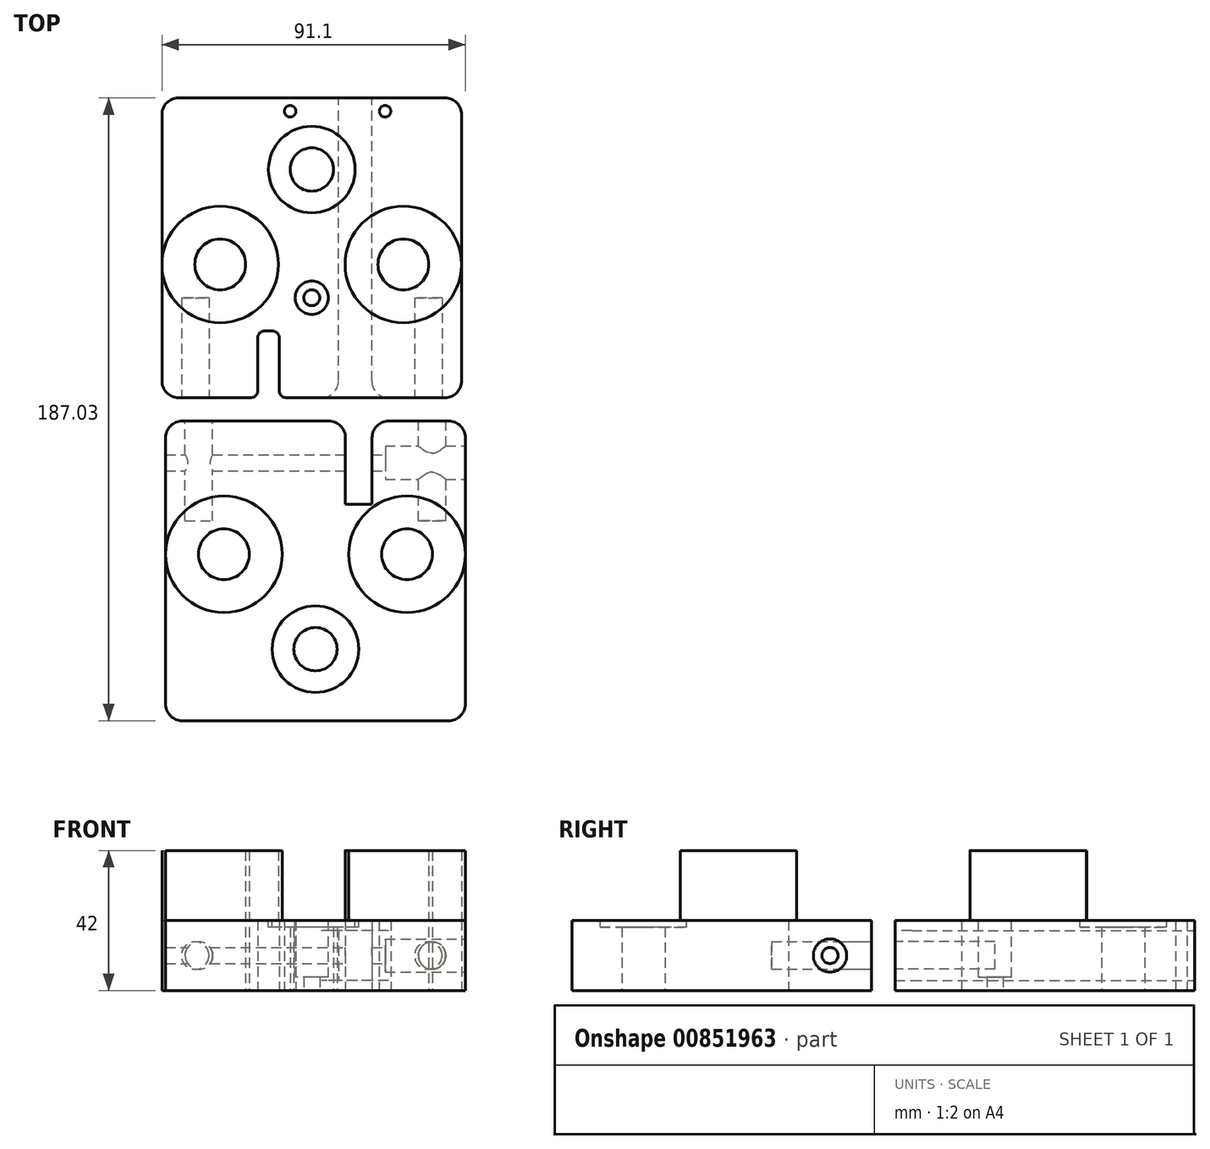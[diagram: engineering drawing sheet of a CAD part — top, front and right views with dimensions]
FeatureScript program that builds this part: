
annotation { "Feature Type Name" : "Feature", "Feature Type Description" : "" }
export const myFeature = defineFeature(function(context is Context, id is Id, definition is map)
    precondition{}
    {
        {
            var Q0;
            Q0=qCreatedBy(makeId("Top.planeOp"),FACE);
            var sketch = newSketch(context, id + "F0", { "sketchPlane" : qUnion([Q0])});
            skLineSegment(sketch, "E0", {"start": v(27.5, 0) * mm, "end": v(-27.5, 0) * mm, "construction": true});
            skCircle(sketch, "E1", {"center": v(-27.5, 0) * mm, "radius": 7.62 * mm});
            skCircle(sketch, "E2", {"center": v(27.5, 0) * mm, "radius": 7.62 * mm});
            skLineSegment(sketch, "E3", {"start": v(0, 28.5) * mm, "end": v(0, -10) * mm, "construction": true});
            skCircle(sketch, "E4", {"center": v(0, 28.5) * mm, "radius": 6.5 * mm});
            skCircle(sketch, "E5", {"center": v(0, 28.5) * mm, "radius": 13 * mm, "construction": true});
            skCircle(sketch, "E6", {"center": v(0, -10) * mm, "radius": 2.4 * mm});
            skCircle(sketch, "E7", {"center": v(0, -10) * mm, "radius": 5 * mm, "construction": true});
            skLineSegment(sketch, "E8", {"start": v(-45, -40) * mm, "end": v(-16.25, -40) * mm});
            skLineSegment(sketch, "E9", {"start": v(0, -10) * mm, "end": v(0, -40) * mm, "construction": true});
            skLineSegment(sketch, "E10", {"start": v(35, -40) * mm, "end": v(35, -10) * mm, "construction": true});
            skLineSegment(sketch, "E11", {"start": v(-35, -40) * mm, "end": v(-35, -10) * mm, "construction": true});
            skLineSegment(sketch, "E12", {"start": v(-45, -40) * mm, "end": v(-45, 50) * mm});
            skLineSegment(sketch, "E13", {"start": v(45, -40) * mm, "end": v(45, 50) * mm});
            skLineSegment(sketch, "E14", {"start": v(13, -40) * mm, "end": v(13, 50) * mm, "construction": true});
            skLineSegment(sketch, "E15", {"start": v(-13, -40) * mm, "end": v(-13, 50) * mm, "construction": true});
            skLineSegment(sketch, "E16", {"start": v(-45, 50) * mm, "end": v(45, 50) * mm});
            skLineSegment(sketch, "E17", {"start": v(-6.5, 46) * mm, "end": v(22, 46) * mm, "construction": true});
            skCircle(sketch, "E18", {"center": v(22, 46) * mm, "radius": 1.72 * mm});
            skCircle(sketch, "E19", {"center": v(-6.5, 46) * mm, "radius": 1.72 * mm});
            skLineSegment(sketch, "E20", {"start": v(-9.75, -20) * mm, "end": v(-16.25, -20) * mm});
            skPoint(sketch, "E21", {"position": v(-13, -20) * mm});
            skLineSegment(sketch, "E22", {"start": v(-16.25, -20) * mm, "end": v(-16.25, -40) * mm});
            skLineSegment(sketch, "E23", {"start": v(-9.75, -20) * mm, "end": v(-9.75, -40) * mm});
            skLineSegment(sketch, "E24.trimOffspring", {"start": v(-9.75, -40) * mm, "end": v(45, -40) * mm});
            skSolve(sketch);
        }
        {
            var Q0;
            Q0 = qSketchRegion(id + "F0", true);
            extrude(context, id + "F1", {"entities" : qUnion([Q0]), "depth" : 21 * mm, "offsetDistance" : 25 * mm});
        }
        {
            var Q0;
            Q0=makeQuery(id+"F1.opExtrude","CAP_FACE",FACE,{"disambiguationData":[OSD([sQuery(id+"F0.wireOp",EDGE,"E1"),sQuery(id+"F0.wireOp",EDGE,"E2"),sQuery(id+"F0.wireOp",EDGE,"E5"),sQuery(id+"F0.wireOp",EDGE,"E6"),sQuery(id+"F0.wireOp",EDGE,"E8"),sQuery(id+"F0.wireOp",EDGE,"E12"),sQuery(id+"F0.wireOp",EDGE,"E13"),sQuery(id+"F0.wireOp",EDGE,"E16"),sQuery(id+"F0.wireOp",EDGE,"E18"),sQuery(id+"F0.wireOp",EDGE,"E19")])],"isStart":false});
            var sketch = newSketch(context, id + "F2", { "sketchPlane" : qUnion([Q0])});
            skCircle(sketch, "E25.0", {"center": v(0, -10) * mm, "radius": 5 * mm});
            skSolve(sketch);
        }
        {
            var Q0;
            Q0=makeQuery(id+"F2.imprint","IMPRINT",FACE,{"disambiguationData":[TD([[makeQuery(id+"F2.imprint","IMPRINT",EDGE,{"derivedFrom":sQuery(id+"F2.wireOp",EDGE,"E25.0")}),1.0]])]});
            extrude(context, id + "F3", {"entities" : qUnion([Q0]), "operationType" : NewBodyOperationType.REMOVE, "oppositeDirection" : true, "depth" : 17 * mm, "offsetDistance" : 25 * mm});
        }
        {
            var Q0;
            Q0=makeQuery(id+"F1.opExtrude","CAP_FACE",FACE,{"disambiguationData":[OSD([sQuery(id+"F0.wireOp",EDGE,"E1"),sQuery(id+"F0.wireOp",EDGE,"E2"),sQuery(id+"F0.wireOp",EDGE,"E4"),sQuery(id+"F0.wireOp",EDGE,"E6"),sQuery(id+"F0.wireOp",EDGE,"E8"),sQuery(id+"F0.wireOp",EDGE,"E12"),sQuery(id+"F0.wireOp",EDGE,"E13"),sQuery(id+"F0.wireOp",EDGE,"E16"),sQuery(id+"F0.wireOp",EDGE,"E18"),sQuery(id+"F0.wireOp",EDGE,"E19")])],"isStart":false});
            var sketch = newSketch(context, id + "F4", { "sketchPlane" : qUnion([Q0])});
            skCircle(sketch, "E26.0", {"center": v(0, 28.5) * mm, "radius": 13 * mm});
            skPoint(sketch, "E27.0", {"position": v(-27.5, 0) * mm});
            skPoint(sketch, "E27.1", {"position": v(27.5, 0) * mm});
            skCircle(sketch, "E28", {"center": v(-27.5, 0) * mm, "radius": 17.5 * mm});
            skCircle(sketch, "E29", {"center": v(27.5, 0) * mm, "radius": 17.49 * mm});
            skLineSegment(sketch, "E30.0", {"start": v(45, -40) * mm, "end": v(45, 50) * mm});
            skSolve(sketch);
        }
        {
            var Q0;
            Q0=makeQuery(id+"F4.imprint","IMPRINT",FACE,{"disambiguationData":[TD([[makeQuery(id+"F4.imprint","IMPRINT",EDGE,{"derivedFrom":sQuery(id+"F4.wireOp",EDGE,"E28")}),1.0]])]});
            var Q1;
            Q1=makeQuery(id+"F4.imprint","IMPRINT",FACE,{"disambiguationData":[TD([[makeQuery(id+"F4.imprint","IMPRINT",EDGE,{"derivedFrom":makeQuery(id+"F1.opExtrude","CAP_EDGE",EDGE,{"disambiguationData":[OSD([sQuery(id+"F0.wireOp",EDGE,"E2")])],"isStart":false})}),-1.0]])]});
            extrude(context, id + "F5", {"entities" : qUnion([Q0, Q1]), "operationType" : NewBodyOperationType.ADD, "depth" : 21 * mm, "offsetDistance" : 25 * mm});
        }
        {
            var Q0;
            Q0=makeQuery(id+"F1.opExtrude","SWEPT_FACE",FACE,{"disambiguationData":[OSD([sQuery(id+"F0.wireOp",EDGE,"E16")])]});
            var sketch = newSketch(context, id + "F6", { "sketchPlane" : qUnion([Q0])});
            skPoint(sketch, "E31.0", {"position": v(-13, 0) * mm});
            skLineSegment(sketch, "E32.bottom", {"start": v(-18, 18) * mm, "end": v(-8, 18) * mm});
            skLineSegment(sketch, "E32.top", {"start": v(-18, 3) * mm, "end": v(-8, 3) * mm});
            skLineSegment(sketch, "E32.left", {"start": v(-18, 18) * mm, "end": v(-18, 3) * mm});
            skLineSegment(sketch, "E32.right", {"start": v(-8, 18) * mm, "end": v(-8, 3) * mm});
            skLineSegment(sketch, "E33.0", {"start": v(45, 21) * mm, "end": v(-45, 21) * mm});
            skLineSegment(sketch, "E34", {"start": v(-13, 0) * mm, "end": v(-13, 21) * mm, "construction": true});
            skPoint(sketch, "E35", {"position": v(-13, 18) * mm});
            skPoint(sketch, "E36", {"position": v(-13, 3) * mm});
            skSolve(sketch);
        }
        {
            var Q0;
            Q0=makeQuery(id+"F6.imprint","IMPRINT",FACE,{"disambiguationData":[TD([[makeQuery(id+"F6.imprint","IMPRINT",EDGE,{"derivedFrom":sQuery(id+"F6.wireOp",EDGE,"E32.bottom")}),-1.0]])]});
            extrude(context, id + "F7", {"entities" : qUnion([Q0]), "operationType" : NewBodyOperationType.REMOVE, "endBound" : BoundingType.THROUGH_ALL, "oppositeDirection" : true, "depth" : 25 * mm, "offsetDistance" : 25 * mm});
        }
        {
            var Q0;
            Q0=makeQuery(id+"F0.imprint","IMPRINT",FACE,{"disambiguationData":[TD([[makeQuery(id+"F0.imprint","IMPRINT",EDGE,{"derivedFrom":sQuery(id+"F0.wireOp",EDGE,"E1")}),-1.0]])]});
            var sketch = newSketch(context, id + "F8", { "sketchPlane" : qUnion([Q0])});
            skCircle(sketch, "E37.0", {"center": v(0, 28.5) * mm, "radius": 13 * mm});
            skSolve(sketch);
        }
        {
            var Q0;
            Q0=makeQuery(id+"F1.opExtrude","SWEPT_FACE",FACE,{"disambiguationData":[OSD([sQuery(id+"F0.wireOp",EDGE,"E8")])]});
            var sketch = newSketch(context, id + "F9", { "sketchPlane" : qUnion([Q0])});
            skLineSegment(sketch, "E38.0", {"start": v(-45, 21) * mm, "end": v(45, 21) * mm});
            skPoint(sketch, "E39.0", {"position": v(-35, 0) * mm});
            skPoint(sketch, "E40.0", {"position": v(35, 0) * mm});
            skLineSegment(sketch, "E41.0", {"start": v(-45, 0) * mm, "end": v(45, 0) * mm});
            skLineSegment(sketch, "E42", {"start": v(-35, 0) * mm, "end": v(-35, 21) * mm, "construction": true});
            skLineSegment(sketch, "E43", {"start": v(35, 0) * mm, "end": v(35, 21) * mm, "construction": true});
            skCircle(sketch, "E44", {"center": v(-35, 10.5) * mm, "radius": 4.12 * mm});
            skCircle(sketch, "E45", {"center": v(35, 10.5) * mm, "radius": 4.12 * mm});
            skSolve(sketch);
        }
        {
            var Q0;
            Q0=makeQuery(id+"F9.imprint","IMPRINT",FACE,{"disambiguationData":[TD([[makeQuery(id+"F9.imprint","IMPRINT",EDGE,{"derivedFrom":sQuery(id+"F9.wireOp",EDGE,"E44")}),1.0]])]});
            var Q1;
            Q1=makeQuery(id+"F9.imprint","IMPRINT",FACE,{"disambiguationData":[TD([[makeQuery(id+"F9.imprint","IMPRINT",EDGE,{"derivedFrom":sQuery(id+"F9.wireOp",EDGE,"E45")}),1.0]])]});
            extrude(context, id + "F10", {"entities" : qUnion([Q0, Q1]), "operationType" : NewBodyOperationType.REMOVE, "oppositeDirection" : true, "depth" : 30 * mm, "offsetDistance" : 25 * mm});
        }
        {
            var Q0;
            Q0=makeQuery(id+"F1.opExtrude","SWEPT_EDGE",EDGE,{"disambiguationData":[OSD([sQuery(id+"F0.wireOp",EDGE,"E8"),sQuery(id+"F0.wireOp",EDGE,"E12")])]});
            var Q1;
            Q1=makeQuery(id+"F1.opExtrude","SWEPT_EDGE",EDGE,{"disambiguationData":[OSD([sQuery(id+"F0.wireOp",EDGE,"E13"),sQuery(id+"F0.wireOp",EDGE,"E24.trimOffspring")])]});
            var Q2;
            Q2=makeQuery(id+"F1.opExtrude","SWEPT_EDGE",EDGE,{"disambiguationData":[OSD([sQuery(id+"F0.wireOp",EDGE,"E13"),sQuery(id+"F0.wireOp",EDGE,"E16")])]});
            var Q3;
            Q3=makeQuery(id+"F7.boolean.opBoolean","INTERSECT",EDGE,{"derivedFrom":[makeQuery(id+"F1.opExtrude","SWEPT_FACE",FACE,{"disambiguationData":[OSD([sQuery(id+"F0.wireOp",EDGE,"E24.trimOffspring")])]}),makeQuery(id+"F7.opExtrude","SWEPT_FACE",FACE,{"disambiguationData":[OSD([sQuery(id+"F6.wireOp",EDGE,"E32.right")])]})]});
            var Q4;
            Q4=makeQuery(id+"F7.boolean.opBoolean","INTERSECT",EDGE,{"derivedFrom":[makeQuery(id+"F1.opExtrude","SWEPT_FACE",FACE,{"disambiguationData":[OSD([sQuery(id+"F0.wireOp",EDGE,"E24.trimOffspring")])]}),makeQuery(id+"F7.opExtrude","SWEPT_FACE",FACE,{"disambiguationData":[OSD([sQuery(id+"F6.wireOp",EDGE,"E32.left")])]})]});
            var Q5;
            Q5=makeQuery(id+"F7.boolean.opBoolean","COPY",EDGE,{"derivedFrom":makeQuery(id+"F7.opExtrude","CAP_EDGE",EDGE,{"disambiguationData":[OSD([sQuery(id+"F6.wireOp",EDGE,"E32.right")])],"isStart":true})});
            var Q6;
            Q6=makeQuery(id+"F7.boolean.opBoolean","COPY",EDGE,{"derivedFrom":makeQuery(id+"F7.opExtrude","CAP_EDGE",EDGE,{"disambiguationData":[OSD([sQuery(id+"F6.wireOp",EDGE,"E32.left")])],"isStart":true})});
            var Q7;
            Q7=makeQuery(id+"F1.opExtrude","SWEPT_EDGE",EDGE,{"disambiguationData":[OSD([sQuery(id+"F0.wireOp",EDGE,"E12"),sQuery(id+"F0.wireOp",EDGE,"E16")])]});
            fillet(context, id + "F11", {"entities" : qUnion([Q0, Q1, Q2, Q3, Q4, Q5, Q6, Q7]), "radius" : 5 * mm, "tangentPropagation" : true, "allowEdgeOverflow" : false});
        }
        {
            var Q0;
            Q0=makeQuery(id+"F4.imprint","IMPRINT",FACE,{"disambiguationData":[TD([[makeQuery(id+"F4.imprint","IMPRINT",EDGE,{"derivedFrom":sQuery(id+"F4.wireOp",EDGE,"E26.0")}),1.0]])]});
            extrude(context, id + "F12", {"entities" : qUnion([Q0]), "operationType" : NewBodyOperationType.REMOVE, "oppositeDirection" : true, "depth" : 2 * mm, "offsetDistance" : 25 * mm});
        }
        {
            var Q0;
            Q0=makeQuery(id+"F1.opExtrude","SWEPT_EDGE",EDGE,{"disambiguationData":[OSD([sQuery(id+"F0.wireOp",EDGE,"E8"),sQuery(id+"F0.wireOp",EDGE,"E22")])]});
            var Q1;
            Q1=makeQuery(id+"F1.opExtrude","SWEPT_EDGE",EDGE,{"disambiguationData":[OSD([sQuery(id+"F0.wireOp",EDGE,"E23"),sQuery(id+"F0.wireOp",EDGE,"E24.trimOffspring")])]});
            var Q2;
            Q2=makeQuery(id+"F1.opExtrude","SWEPT_EDGE",EDGE,{"disambiguationData":[OSD([sQuery(id+"F0.wireOp",EDGE,"E20"),sQuery(id+"F0.wireOp",EDGE,"E23")])]});
            var Q3;
            Q3=makeQuery(id+"F1.opExtrude","SWEPT_EDGE",EDGE,{"disambiguationData":[OSD([sQuery(id+"F0.wireOp",EDGE,"E20"),sQuery(id+"F0.wireOp",EDGE,"E22")])]});
            fillet(context, id + "F13", {"entities" : qUnion([Q0, Q1, Q2, Q3]), "radius" : 2 * mm, "tangentPropagation" : true, "allowEdgeOverflow" : false});
        }
        {
            var Q0;
            Q0=qCreatedBy(makeId("Top.planeOp"),FACE);
            var sketch = newSketch(context, id + "F14", { "sketchPlane" : qUnion([Q0])});
            skLineSegment(sketch, "E46", {"start": v(-26.4, -87.03) * mm, "end": v(28.6, -87.03) * mm, "construction": true});
            skCircle(sketch, "E47", {"center": v(28.6, -87.03) * mm, "radius": 7.62 * mm});
            skCircle(sketch, "E48", {"center": v(-26.4, -87.03) * mm, "radius": 7.62 * mm});
            skLineSegment(sketch, "E49", {"start": v(1.1, -115.53) * mm, "end": v(1.1, -77.03) * mm, "construction": true});
            skCircle(sketch, "E50", {"center": v(1.1, -115.53) * mm, "radius": 6.5 * mm});
            skCircle(sketch, "E51", {"center": v(1.1, -115.53) * mm, "radius": 13 * mm, "construction": true});
            skLineSegment(sketch, "E52", {"start": v(46.1, -47.03) * mm, "end": v(18.1, -47.03) * mm});
            skLineSegment(sketch, "E53", {"start": v(1.1, -77.03) * mm, "end": v(1.1, -47.03) * mm, "construction": true});
            skLineSegment(sketch, "E54", {"start": v(-33.9, -47.03) * mm, "end": v(-33.9, -77.03) * mm, "construction": true});
            skLineSegment(sketch, "E55", {"start": v(36.1, -47.03) * mm, "end": v(36.1, -77.03) * mm, "construction": true});
            skLineSegment(sketch, "E56", {"start": v(46.1, -47.03) * mm, "end": v(46.1, -137.03) * mm});
            skLineSegment(sketch, "E57", {"start": v(-43.9, -47.03) * mm, "end": v(-43.9, -137.03) * mm});
            skLineSegment(sketch, "E58", {"start": v(14.1, -47.03) * mm, "end": v(14.1, -137.03) * mm, "construction": true});
            skLineSegment(sketch, "E59", {"start": v(46.1, -137.03) * mm, "end": v(-43.9, -137.03) * mm});
            skLineSegment(sketch, "E60", {"start": v(10.1, -72.03) * mm, "end": v(18.1, -72.03) * mm});
            skPoint(sketch, "E61", {"position": v(14.1, -72.03) * mm});
            skLineSegment(sketch, "E62", {"start": v(18.1, -72.03) * mm, "end": v(18.1, -47.03) * mm});
            skLineSegment(sketch, "E63", {"start": v(10.1, -72.03) * mm, "end": v(10.1, -47.03) * mm});
            skLineSegment(sketch, "E64.trimOffspring", {"start": v(10.1, -47.03) * mm, "end": v(-43.9, -47.03) * mm});
            skPoint(sketch, "E65", {"position": v(1.1, -87.03) * mm});
            skLineSegment(sketch, "E66", {"start": v(18.1, -59.53) * mm, "end": v(46.1, -59.53) * mm, "construction": true});
            skLineSegment(sketch, "E67", {"start": v(18.1, -59.53) * mm, "end": v(10.1, -59.53) * mm, "construction": true});
            skLineSegment(sketch, "E68", {"start": v(10.1, -59.53) * mm, "end": v(-43.9, -59.53) * mm, "construction": true});
            skSolve(sketch);
        }
        {
            var Q0;
            Q0 = qSketchRegion(id + "F14", true);
            extrude(context, id + "F15", {"entities" : qUnion([Q0]), "depth" : 21 * mm, "offsetDistance" : 25 * mm});
        }
        {
            var Q0;
            Q0=makeQuery(id+"F15.opExtrude","SWEPT_EDGE",EDGE,{"disambiguationData":[OSD([sQuery(id+"F14.wireOp",EDGE,"E52"),sQuery(id+"F14.wireOp",EDGE,"E62")])]});
            var Q1;
            Q1=makeQuery(id+"F15.opExtrude","SWEPT_EDGE",EDGE,{"disambiguationData":[OSD([sQuery(id+"F14.wireOp",EDGE,"E57"),sQuery(id+"F14.wireOp",EDGE,"E64.trimOffspring")])]});
            var Q2;
            Q2=makeQuery(id+"F15.opExtrude","SWEPT_EDGE",EDGE,{"disambiguationData":[OSD([sQuery(id+"F14.wireOp",EDGE,"E63"),sQuery(id+"F14.wireOp",EDGE,"E64.trimOffspring")])]});
            var Q3;
            Q3=makeQuery(id+"F15.opExtrude","SWEPT_EDGE",EDGE,{"disambiguationData":[OSD([sQuery(id+"F14.wireOp",EDGE,"E57"),sQuery(id+"F14.wireOp",EDGE,"E59")])]});
            var Q4;
            Q4=makeQuery(id+"F15.opExtrude","SWEPT_EDGE",EDGE,{"disambiguationData":[OSD([sQuery(id+"F14.wireOp",EDGE,"E56"),sQuery(id+"F14.wireOp",EDGE,"E59")])]});
            var Q5;
            Q5=makeQuery(id+"F15.opExtrude","SWEPT_EDGE",EDGE,{"disambiguationData":[OSD([sQuery(id+"F14.wireOp",EDGE,"E52"),sQuery(id+"F14.wireOp",EDGE,"E56")])]});
            fillet(context, id + "F16", {"entities" : qUnion([Q0, Q1, Q2, Q3, Q4, Q5]), "radius" : 5 * mm, "tangentPropagation" : true, "allowEdgeOverflow" : false});
        }
        {
            var Q0;
            Q0=makeQuery(id+"F15.opExtrude","CAP_FACE",FACE,{"disambiguationData":[OSD([sQuery(id+"F14.wireOp",EDGE,"E47"),sQuery(id+"F14.wireOp",EDGE,"E48"),sQuery(id+"F14.wireOp",EDGE,"E50"),sQuery(id+"F14.wireOp",EDGE,"E52"),sQuery(id+"F14.wireOp",EDGE,"E56"),sQuery(id+"F14.wireOp",EDGE,"E57"),sQuery(id+"F14.wireOp",EDGE,"E59"),sQuery(id+"F14.wireOp",EDGE,"E60"),sQuery(id+"F14.wireOp",EDGE,"E62"),sQuery(id+"F14.wireOp",EDGE,"E63"),sQuery(id+"F14.wireOp",EDGE,"E64.trimOffspring")])],"isStart":false});
            var sketch = newSketch(context, id + "F17", { "sketchPlane" : qUnion([Q0])});
            skCircle(sketch, "E69.0", {"center": v(1.1, -115.53) * mm, "radius": 13 * mm});
            skSolve(sketch);
        }
        {
            var Q0;
            Q0=makeQuery(id+"F17.imprint","IMPRINT",FACE,{"disambiguationData":[TD([[makeQuery(id+"F17.imprint","IMPRINT",EDGE,{"derivedFrom":sQuery(id+"F17.wireOp",EDGE,"E69.0")}),1.0]])]});
            extrude(context, id + "F18", {"entities" : qUnion([Q0]), "operationType" : NewBodyOperationType.REMOVE, "oppositeDirection" : true, "depth" : 2 * mm, "offsetDistance" : 25 * mm});
        }
        {
            var Q0;
            Q0=makeQuery(id+"F15.opExtrude","CAP_FACE",FACE,{"disambiguationData":[OSD([sQuery(id+"F14.wireOp",EDGE,"E47"),sQuery(id+"F14.wireOp",EDGE,"E48"),sQuery(id+"F14.wireOp",EDGE,"E50"),sQuery(id+"F14.wireOp",EDGE,"E52"),sQuery(id+"F14.wireOp",EDGE,"E56"),sQuery(id+"F14.wireOp",EDGE,"E57"),sQuery(id+"F14.wireOp",EDGE,"E59"),sQuery(id+"F14.wireOp",EDGE,"E60"),sQuery(id+"F14.wireOp",EDGE,"E62"),sQuery(id+"F14.wireOp",EDGE,"E63"),sQuery(id+"F14.wireOp",EDGE,"E64.trimOffspring")])],"isStart":false});
            var sketch = newSketch(context, id + "F19", { "sketchPlane" : qUnion([Q0])});
            skPoint(sketch, "E70.0", {"position": v(-26.4, -87.03) * mm});
            skPoint(sketch, "E71.0", {"position": v(28.6, -87.03) * mm});
            skCircle(sketch, "E72", {"center": v(-26.4, -87.03) * mm, "radius": 17.5 * mm});
            skCircle(sketch, "E73", {"center": v(28.6, -87.03) * mm, "radius": 17.5 * mm});
            skSolve(sketch);
        }
        {
            var Q0;
            Q0=makeQuery(id+"F19.imprint","IMPRINT",FACE,{"disambiguationData":[TD([[makeQuery(id+"F19.imprint","IMPRINT",EDGE,{"derivedFrom":sQuery(id+"F19.wireOp",EDGE,"E73")}),1.0]])]});
            var Q1;
            Q1=makeQuery(id+"F19.imprint","IMPRINT",FACE,{"disambiguationData":[TD([[makeQuery(id+"F19.imprint","IMPRINT",EDGE,{"derivedFrom":sQuery(id+"F19.wireOp",EDGE,"E72")}),1.0]])]});
            extrude(context, id + "F20", {"entities" : qUnion([Q0, Q1]), "operationType" : NewBodyOperationType.ADD, "depth" : 21 * mm, "offsetDistance" : 25 * mm});
        }
        {
            var Q0;
            Q0=makeQuery(id+"F15.opExtrude","SWEPT_FACE",FACE,{"disambiguationData":[OSD([sQuery(id+"F14.wireOp",EDGE,"E56")])]});
            var sketch = newSketch(context, id + "F21", { "sketchPlane" : qUnion([Q0])});
            skPoint(sketch, "E74.0", {"position": v(-59.53, 0) * mm});
            skLineSegment(sketch, "E75", {"start": v(-59.53, 0) * mm, "end": v(-59.53, 21) * mm, "construction": true});
            skCircle(sketch, "E76", {"center": v(-59.53, 10.5) * mm, "radius": 2.4 * mm});
            skCircle(sketch, "E77", {"center": v(-59.53, 10.5) * mm, "radius": 5 * mm});
            skSolve(sketch);
        }
        {
            var Q0;
            Q0=makeQuery(id+"F21.imprint","IMPRINT",FACE,{"disambiguationData":[TD([[makeQuery(id+"F21.imprint","IMPRINT",EDGE,{"derivedFrom":sQuery(id+"F21.wireOp",EDGE,"E76")}),1.0]])]});
            var Q1;
            Q1=makeQuery(id+"F21.imprint","IMPRINT",FACE,{"disambiguationData":[TD([[makeQuery(id+"F21.imprint","IMPRINT",EDGE,{"derivedFrom":sQuery(id+"F21.wireOp",EDGE,"E76")}),-1.0]])]});
            extrude(context, id + "F22", {"entities" : qUnion([Q0, Q1]), "operationType" : NewBodyOperationType.REMOVE, "oppositeDirection" : true, "depth" : 24 * mm, "offsetDistance" : 25 * mm});
        }
        {
            var Q0;
            Q0=makeQuery(id+"F21.imprint","IMPRINT",FACE,{"disambiguationData":[TD([[makeQuery(id+"F21.imprint","IMPRINT",EDGE,{"derivedFrom":sQuery(id+"F21.wireOp",EDGE,"E76")}),1.0]])]});
            extrude(context, id + "F23", {"entities" : qUnion([Q0]), "operationType" : NewBodyOperationType.REMOVE, "endBound" : BoundingType.THROUGH_ALL, "oppositeDirection" : true, "depth" : 25 * mm, "offsetDistance" : 25 * mm});
        }
        {
            var Q0;
            Q0=makeQuery(id+"F15.opExtrude","SWEPT_FACE",FACE,{"disambiguationData":[OSD([sQuery(id+"F14.wireOp",EDGE,"E64.trimOffspring")])]});
            var sketch = newSketch(context, id + "F24", { "sketchPlane" : qUnion([Q0])});
            skPoint(sketch, "E78.0", {"position": v(33.9, 0) * mm});
            skLineSegment(sketch, "E79", {"start": v(33.9, 0) * mm, "end": v(33.9, 21) * mm, "construction": true});
            skCircle(sketch, "E80", {"center": v(33.9, 10.5) * mm, "radius": 4.12 * mm});
            skSolve(sketch);
        }
        {
            var Q0;
            Q0=makeQuery(id+"F15.opExtrude","SWEPT_FACE",FACE,{"disambiguationData":[OSD([sQuery(id+"F14.wireOp",EDGE,"E52")])]});
            var sketch = newSketch(context, id + "F25", { "sketchPlane" : qUnion([Q0])});
            skPoint(sketch, "E81.0", {"position": v(-36.1, 0) * mm});
            skLineSegment(sketch, "E82", {"start": v(-36.1, 0) * mm, "end": v(-36.1, 21) * mm, "construction": true});
            skCircle(sketch, "E83", {"center": v(-36.1, 10.5) * mm, "radius": 4.12 * mm});
            skSolve(sketch);
        }
        {
            var Q0;
            Q0=makeQuery(id+"F25.imprint","IMPRINT",FACE,{"disambiguationData":[TD([[makeQuery(id+"F25.imprint","IMPRINT",EDGE,{"derivedFrom":sQuery(id+"F25.wireOp",EDGE,"E83")}),1.0]])]});
            var Q1;
            Q1=makeQuery(id+"F24.imprint","IMPRINT",FACE,{"disambiguationData":[TD([[makeQuery(id+"F24.imprint","IMPRINT",EDGE,{"derivedFrom":sQuery(id+"F24.wireOp",EDGE,"E80")}),1.0]])]});
            extrude(context, id + "F26", {"entities" : qUnion([Q0, Q1]), "operationType" : NewBodyOperationType.REMOVE, "oppositeDirection" : true, "depth" : 30 * mm, "offsetDistance" : 25 * mm});
        }
    });
